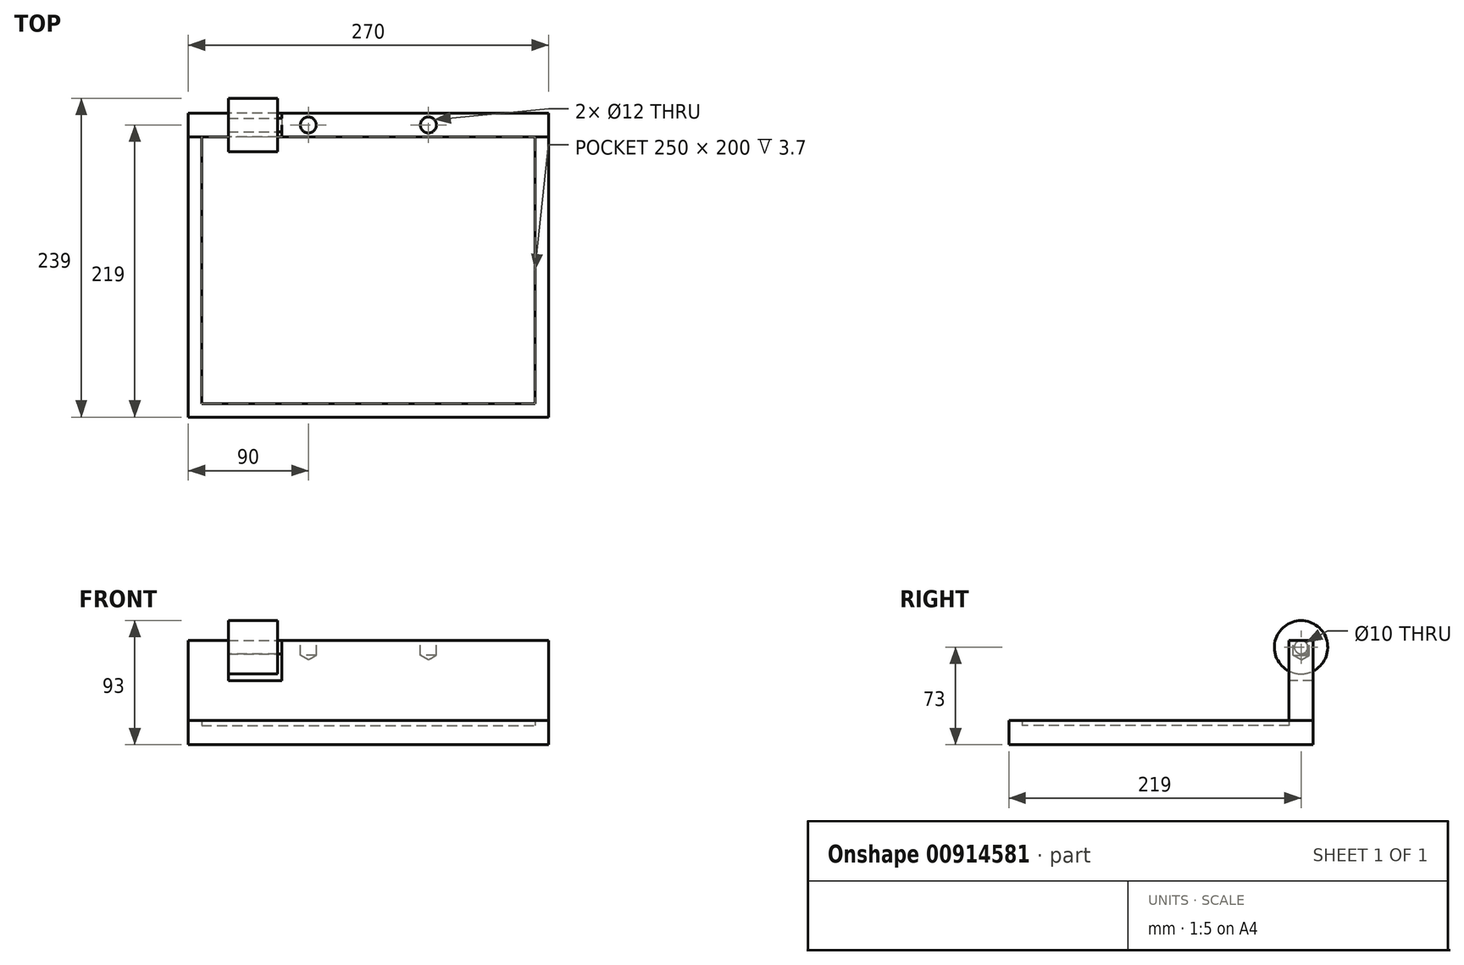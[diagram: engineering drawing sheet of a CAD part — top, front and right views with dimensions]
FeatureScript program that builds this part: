
annotation { "Feature Type Name" : "Feature", "Feature Type Description" : "" }
export const myFeature = defineFeature(function(context is Context, id is Id, definition is map)
    precondition{}
    {
        {
            var Q0;
            Q0=qCreatedBy(makeId("Top.planeOp"),FACE);
            var sketch = newSketch(context, id + "F0", { "sketchPlane" : qUnion([Q0])});
            skLineSegment(sketch, "E0.bottom", {"start": v(125, -100) * mm, "end": v(-125, -100) * mm});
            skLineSegment(sketch, "E0.top", {"start": v(125, 100) * mm, "end": v(-125, 100) * mm});
            skLineSegment(sketch, "E0.left", {"start": v(125, -100) * mm, "end": v(125, 100) * mm});
            skLineSegment(sketch, "E0.right", {"start": v(-125, -100) * mm, "end": v(-125, 100) * mm});
            skPoint(sketch, "E0.middle", {"position": v(0, 0) * mm});
            skLineSegment(sketch, "E1.bottom", {"start": v(135, -110) * mm, "end": v(-135, -110) * mm});
            skLineSegment(sketch, "E1.top", {"start": v(135, 118) * mm, "end": v(-135, 118) * mm});
            skLineSegment(sketch, "E1.left", {"start": v(135, -110) * mm, "end": v(135, 118) * mm});
            skLineSegment(sketch, "E1.right", {"start": v(-135, -110) * mm, "end": v(-135, 118) * mm});
            skPoint(sketch, "E1.middle", {"position": v(0, 4) * mm});
            skSolve(sketch);
        }
        {
            var Q0;
            Q0 = qSketchRegion(id + "F0", true);
            var Q1;
            Q1=makeQuery(id+"F0.imprint","IMPRINT",FACE,{"disambiguationData":[TD([[makeQuery(id+"F0.imprint","IMPRINT",EDGE,{"derivedFrom":sQuery(id+"F0.wireOp",EDGE,"E0.bottom")}),-1.0]])]});
            extrude(context, id + "F1", {"entities" : qUnion([Q0, Q1]), "depth" : (18 - 3.7) * mm, "offsetDistance" : 25 * mm});
        }
        {
            var Q0;
            Q0=makeQuery(id+"F0.imprint","IMPRINT",FACE,{"disambiguationData":[TD([[makeQuery(id+"F0.imprint","IMPRINT",EDGE,{"derivedFrom":sQuery(id+"F0.wireOp",EDGE,"E0.bottom")}),1.0]])]});
            extrude(context, id + "F2", {"entities" : qUnion([Q0]), "operationType" : NewBodyOperationType.ADD, "depth" : 18 * mm, "offsetDistance" : 25 * mm});
        }
        {
            var Q0;
            Q0=makeQuery(id+"F2.opExtrude","CAP_FACE",FACE,{"disambiguationData":[OSD([sQuery(id+"F0.wireOp",EDGE,"E0.bottom"),sQuery(id+"F0.wireOp",EDGE,"E0.top"),sQuery(id+"F0.wireOp",EDGE,"E0.left"),sQuery(id+"F0.wireOp",EDGE,"E0.right"),sQuery(id+"F0.wireOp",EDGE,"E1.bottom"),sQuery(id+"F0.wireOp",EDGE,"E1.top"),sQuery(id+"F0.wireOp",EDGE,"E1.left"),sQuery(id+"F0.wireOp",EDGE,"E1.right")])],"isStart":false});
            var sketch = newSketch(context, id + "F3", { "sketchPlane" : qUnion([Q0])});
            skLineSegment(sketch, "E2.bottom", {"start": v(-135, 118) * mm, "end": v(135, 118) * mm});
            skLineSegment(sketch, "E2.top", {"start": v(-135, 100) * mm, "end": v(135, 100) * mm});
            skLineSegment(sketch, "E2.left", {"start": v(-135, 118) * mm, "end": v(-135, 100) * mm});
            skLineSegment(sketch, "E2.right", {"start": v(135, 118) * mm, "end": v(135, 100) * mm});
            skSolve(sketch);
        }
        {
            var Q0;
            Q0 = qSketchRegion(id + "F3", true);
            extrude(context, id + "F4", {"entities" : qUnion([Q0]), "depth" : 60 * mm, "offsetDistance" : 25 * mm});
        }
        {
            var Q0;
            Q0=makeQuery(id+"F4.opExtrude","CAP_FACE",FACE,{"disambiguationData":[OSD([sQuery(id+"F3.wireOp",EDGE,"E2.bottom"),sQuery(id+"F3.wireOp",EDGE,"E2.top"),sQuery(id+"F3.wireOp",EDGE,"E2.left"),sQuery(id+"F3.wireOp",EDGE,"E2.right")])],"isStart":false});
            var sketch = newSketch(context, id + "F5", { "sketchPlane" : qUnion([Q0])});
            skLineSegment(sketch, "E3", {"start": v(-105, 109) * mm, "end": v(-65, 109) * mm, "construction": true});
            skArc(sketch, "E4.0.startCap", {"start": v(-105, 104) * mm, "mid": v(-110, 109) * mm, "end": v(-105, 114) * mm});
            skArc(sketch, "E4.0.endCap", {"start": v(-65, 114) * mm, "mid": v(-60, 109) * mm, "end": v(-65, 104) * mm});
            skLineSegment(sketch, "E4.0.left", {"start": v(-105, 114) * mm, "end": v(-65, 114) * mm});
            skLineSegment(sketch, "E4.0.right", {"start": v(-105, 104) * mm, "end": v(-65, 104) * mm});
            skLineSegment(sketch, "E5.bottom", {"start": v(-105, 118) * mm, "end": v(-65, 118) * mm});
            skLineSegment(sketch, "E5.top", {"start": v(-105, 100) * mm, "end": v(-65, 100) * mm});
            skLineSegment(sketch, "E5.left", {"start": v(-105, 118) * mm, "end": v(-105, 100) * mm});
            skLineSegment(sketch, "E5.right", {"start": v(-65, 118) * mm, "end": v(-65, 100) * mm});
            skLineSegment(sketch, "E6", {"start": v(-135, 109) * mm, "end": v(135, 109) * mm, "construction": true});
            skPoint(sketch, "E7", {"position": v(-45, 109) * mm});
            skPoint(sketch, "E8", {"position": v(45, 109) * mm});
            skSolve(sketch);
        }
        {
            var Q0;
            Q0 = qSketchRegion(id + "F5", true);
            extrude(context, id + "F6", {"entities" : qUnion([Q0]), "operationType" : NewBodyOperationType.REMOVE, "oppositeDirection" : true, "depth" : 10 * mm, "offsetDistance" : 25 * mm});
        }
        {
            var Q0;
            {var subQ0=sQuery(id+"F5.wireOp",EDGE,"E4.0.left");Q0=makeQuery(id+"F5.imprint","IMPRINT",FACE,{"disambiguationData":[TD([[makeQuery(id+"F5.imprint","IMPRINT",EDGE,{"derivedFrom":subQ0}),-1.0]])]});}
            var Q1;
            {var subQ0=sQuery(id+"F5.wireOp",EDGE,"E4.0.left");Q1=makeQuery(id+"F5.imprint","IMPRINT",FACE,{"disambiguationData":[TD([[makeQuery(id+"F5.imprint","IMPRINT",EDGE,{"derivedFrom":subQ0}),1.0]])]});}
            var Q2;
            {var subQ0=sQuery(id+"F5.wireOp",EDGE,"E4.0.right");Q2=makeQuery(id+"F5.imprint","IMPRINT",FACE,{"disambiguationData":[TD([[makeQuery(id+"F5.imprint","IMPRINT",EDGE,{"derivedFrom":subQ0}),-1.0]])]});}
            extrude(context, id + "F7", {"entities" : qUnion([Q0, Q1, Q2]), "operationType" : NewBodyOperationType.REMOVE, "oppositeDirection" : true, "depth" : 30 * mm, "offsetDistance" : 25 * mm});
        }
        {
            var Q0;
            {var subQ0=sQuery(id+"F5.wireOp",EDGE,"E4.0.startCap");var subQ1=sQuery(id+"F5.wireOp",EDGE,"E5.left");var subQ2=sQuery(id+"F5.wireOp",EDGE,"E5.bottom");var subQ3=sQuery(id+"F5.wireOp",EDGE,"E5.top");Q0=makeQuery(id+"F7.boolean.opBoolean","SPLIT",FACE,{"disambiguationData":[TD([makeQuery(id+"F6.boolean.opBoolean","COPY",FACE,{"derivedFrom":makeQuery(id+"F6.opExtrude","SWEPT_FACE",FACE,{"disambiguationData":[OSD([subQ0])]})})])],"derivedFrom":makeQuery(id+"F6.boolean.opBoolean","COPY",FACE,{"derivedFrom":makeQuery(id+"F6.opExtrude","CAP_FACE",FACE,{"disambiguationData":[OSD([subQ0,sQuery(id+"F5.wireOp",EDGE,"E4.0.endCap"),subQ2,subQ3,subQ1,sQuery(id+"F5.wireOp",EDGE,"E5.right")])],"isStart":false})})});}
            var Q1;
            {var subQ0=sQuery(id+"F5.wireOp",EDGE,"E4.0.endCap");var subQ1=sQuery(id+"F5.wireOp",EDGE,"E5.right");var subQ2=sQuery(id+"F5.wireOp",EDGE,"E5.bottom");var subQ3=sQuery(id+"F5.wireOp",EDGE,"E5.top");Q1=makeQuery(id+"F7.boolean.opBoolean","SPLIT",FACE,{"disambiguationData":[TD([makeQuery(id+"F6.boolean.opBoolean","COPY",FACE,{"derivedFrom":makeQuery(id+"F6.opExtrude","SWEPT_FACE",FACE,{"disambiguationData":[OSD([subQ0])]})})])],"derivedFrom":makeQuery(id+"F6.boolean.opBoolean","COPY",FACE,{"derivedFrom":makeQuery(id+"F6.opExtrude","CAP_FACE",FACE,{"disambiguationData":[OSD([sQuery(id+"F5.wireOp",EDGE,"E4.0.startCap"),subQ0,subQ2,subQ3,sQuery(id+"F5.wireOp",EDGE,"E5.left"),subQ1])],"isStart":false})})});}
            extrude(context, id + "F8", {"entities" : qUnion([Q0, Q1]), "depth" : 10 * mm, "offsetDistance" : 25 * mm});
        }
        {
            var Q2;
            {var subQ0=sQuery(id+"F5.wireOp",EDGE,"E5.left");var subQ1=sQuery(id+"F5.wireOp",EDGE,"E5.right");var subQ2=sQuery(id+"F5.wireOp",EDGE,"E5.top");var subQ3=sQuery(id+"F5.wireOp",EDGE,"E5.bottom");var subQ4=sQuery(id+"F5.wireOp",EDGE,"E4.0.endCap");var subQ5=sQuery(id+"F5.wireOp",EDGE,"E4.0.startCap");Q2=makeQuery(id+"F8.opExtrude","SWEPT_FACE",FACE,{"disambiguationData":[OSD([subQ5,subQ4,subQ3,subQ2,subQ0,subQ1]),TDD([makeQuery(id+"F7.boolean.opBoolean","INTERSECT",EDGE,{"derivedFrom":[makeQuery(id+"F6.boolean.opBoolean","COPY",FACE,{"derivedFrom":makeQuery(id+"F6.opExtrude","CAP_FACE",FACE,{"disambiguationData":[OSD([subQ5,subQ4,subQ3,subQ2,subQ0,subQ1])],"isStart":false})}),makeQuery(id+"F7.opExtrude","SWEPT_FACE",FACE,{"disambiguationData":[OSD([subQ0])]})]})])]});}
            var Q3;
            {var subQ0=sQuery(id+"F5.wireOp",EDGE,"E5.right");var subQ1=sQuery(id+"F5.wireOp",EDGE,"E5.left");var subQ2=sQuery(id+"F5.wireOp",EDGE,"E5.top");var subQ3=sQuery(id+"F5.wireOp",EDGE,"E5.bottom");var subQ4=sQuery(id+"F5.wireOp",EDGE,"E4.0.endCap");var subQ5=sQuery(id+"F5.wireOp",EDGE,"E4.0.startCap");Q3=makeQuery(id+"F8.opExtrude","SWEPT_FACE",FACE,{"disambiguationData":[OSD([subQ5,subQ4,subQ3,subQ2,subQ1,subQ0]),TDD([makeQuery(id+"F7.boolean.opBoolean","INTERSECT",EDGE,{"derivedFrom":[makeQuery(id+"F6.boolean.opBoolean","COPY",FACE,{"derivedFrom":makeQuery(id+"F6.opExtrude","CAP_FACE",FACE,{"disambiguationData":[OSD([subQ5,subQ4,subQ3,subQ2,subQ1,subQ0])],"isStart":false})}),makeQuery(id+"F7.opExtrude","SWEPT_FACE",FACE,{"disambiguationData":[OSD([subQ0])]})]})])]});}
            loft(context, id + "F9", {"operationType" : NewBodyOperationType.ADD, "sheetProfilesArray" : [{ "sheetProfileEntities" : qUnion([Q2]) }, { "sheetProfileEntities" : qUnion([Q3]) }]});
        }
        {
            var Q0;
            {var subQ0=sQuery(id+"F5.wireOp",EDGE,"E5.right");var subQ1=sQuery(id+"F5.wireOp",EDGE,"E4.0.right");var subQ2=sQuery(id+"F5.wireOp",EDGE,"E4.0.endCap");var subQ3=sQuery(id+"F5.wireOp",EDGE,"E5.left");var subQ4=sQuery(id+"F5.wireOp",EDGE,"E4.0.startCap");Q0=makeQuery(id+"F9.opLoft","SWEPT_EDGE",EDGE,{"disambiguationData":[OSD([subQ4,subQ2,subQ1,subQ3,subQ0]),TDD([makeQuery(id+"F8.opExtrude","CAP_VERTEX",VERTEX,{"disambiguationData":[OSD([subQ4,subQ1,subQ3])],"isStart":false}),makeQuery(id+"F8.opExtrude","CAP_VERTEX",VERTEX,{"disambiguationData":[OSD([subQ2,subQ1,subQ0])],"isStart":false})])]});}
            var Q1;
            {var subQ0=sQuery(id+"F5.wireOp",EDGE,"E5.right");var subQ1=sQuery(id+"F5.wireOp",EDGE,"E4.0.right");var subQ2=sQuery(id+"F5.wireOp",EDGE,"E4.0.endCap");var subQ3=sQuery(id+"F5.wireOp",EDGE,"E5.left");var subQ4=sQuery(id+"F5.wireOp",EDGE,"E4.0.startCap");Q1=makeQuery(id+"F9.opLoft","SWEPT_EDGE",EDGE,{"disambiguationData":[OSD([subQ4,subQ2,subQ1,subQ3,subQ0]),TDD([makeQuery(id+"F8.opExtrude","CAP_VERTEX",VERTEX,{"disambiguationData":[OSD([subQ4,subQ1,subQ3])],"isStart":true}),makeQuery(id+"F8.opExtrude","CAP_VERTEX",VERTEX,{"disambiguationData":[OSD([subQ2,subQ1,subQ0])],"isStart":true})])]});}
            fillet(context, id + "F10", {"entities" : qUnion([Q0, Q1]), "radius" : 5 * mm, "tangentPropagation" : true, "allowEdgeOverflow" : false});
        }
        {
            var Q0;
            {var subQ0=sQuery(id+"F5.wireOp",EDGE,"E5.left");var subQ1=sQuery(id+"F5.wireOp",EDGE,"E4.0.startCap");Q0=makeQuery(id+"F7.boolean.opBoolean","MERGE",FACE,{"derivedFrom":[makeQuery(id+"F6.boolean.opBoolean","COPY",FACE,{"derivedFrom":makeQuery(id+"F6.opExtrude","SWEPT_FACE",FACE,{"disambiguationData":[OSD([subQ0]),TDD([makeQuery(id+"F5.imprint","IMPRINT",EDGE,{"disambiguationData":[TD([[makeQuery(id+"F5.imprint","INTERSECT",VERTEX,{"derivedFrom":[subQ1,sQuery(id+"F5.wireOp",EDGE,"E4.0.left"),subQ0]}),1.0]])],"derivedFrom":subQ0})])]})}),makeQuery(id+"F6.boolean.opBoolean","COPY",FACE,{"derivedFrom":makeQuery(id+"F6.opExtrude","SWEPT_FACE",FACE,{"disambiguationData":[OSD([subQ0]),TDD([makeQuery(id+"F5.imprint","IMPRINT",EDGE,{"disambiguationData":[TD([[makeQuery(id+"F5.imprint","INTERSECT",VERTEX,{"derivedFrom":[subQ1,sQuery(id+"F5.wireOp",EDGE,"E4.0.right"),subQ0]}),-1.0]])],"derivedFrom":subQ0})])]})})],"fromTools":[makeQuery(id+"F7.opExtrude","SWEPT_FACE",FACE,{"disambiguationData":[OSD([subQ0])]})]});}
            var sketch = newSketch(context, id + "F11", { "sketchPlane" : qUnion([Q0])});
            skCircle(sketch, "E9.0", {"center": v(109, 73) * mm, "radius": 5 * mm});
            skCircle(sketch, "E10", {"center": v(109, 73) * mm, "radius": 20 * mm});
            skSolve(sketch);
        }
        {
            var Q0;
            Q0 = qSketchRegion(id + "F11", true);
            extrude(context, id + "F12", {"entities" : qUnion([Q0]), "depth" : 37 * mm, "offsetDistance" : 25 * mm, "hasSecondDirection" : true, "secondDirectionOppositeDirection" : false, "secondDirectionDepth" : 0 * mm});
        }
        {
            var Q0;
            Q0=sQuery(id+"F5.wireOp",VERTEX,"E7");
            var Q1;
            Q1=sQuery(id+"F5.wireOp",VERTEX,"E8");
            var Q2;
            Q2=makeQuery(id+"F4.opExtrude","SWEPT_BODY",BODY,{"disambiguationData":[OSD([sQuery(id+"F3.wireOp",EDGE,"E2.bottom"),sQuery(id+"F3.wireOp",EDGE,"E2.top"),sQuery(id+"F3.wireOp",EDGE,"E2.left"),sQuery(id+"F3.wireOp",EDGE,"E2.right")])]});
            hole(context, id + "F13", {"style" : HoleStyle.SIMPLE, "endStyle" : HoleEndStyle.BLIND, "standardTappedOrClearance" : lookupTablePath({ "standard" : "ISO", "size" : "12", "type" : "Drilled" }), "standardBlindInLast" : lookupTablePath({ "standard" : "ISO", "size" : "12", "type" : "Drilled" }), "holeDiameter" : 12 * mm, "majorDiameter" : 6.35 * mm, "holeDepth" : 10.9 * mm, "isTappedThrough" : true, "tappedDepth" : 7.1 * mm, "tapClearance" : 3, "locations" : qUnion([Q0, Q1]), "scope" : qUnion([Q2])});
        }
    });
